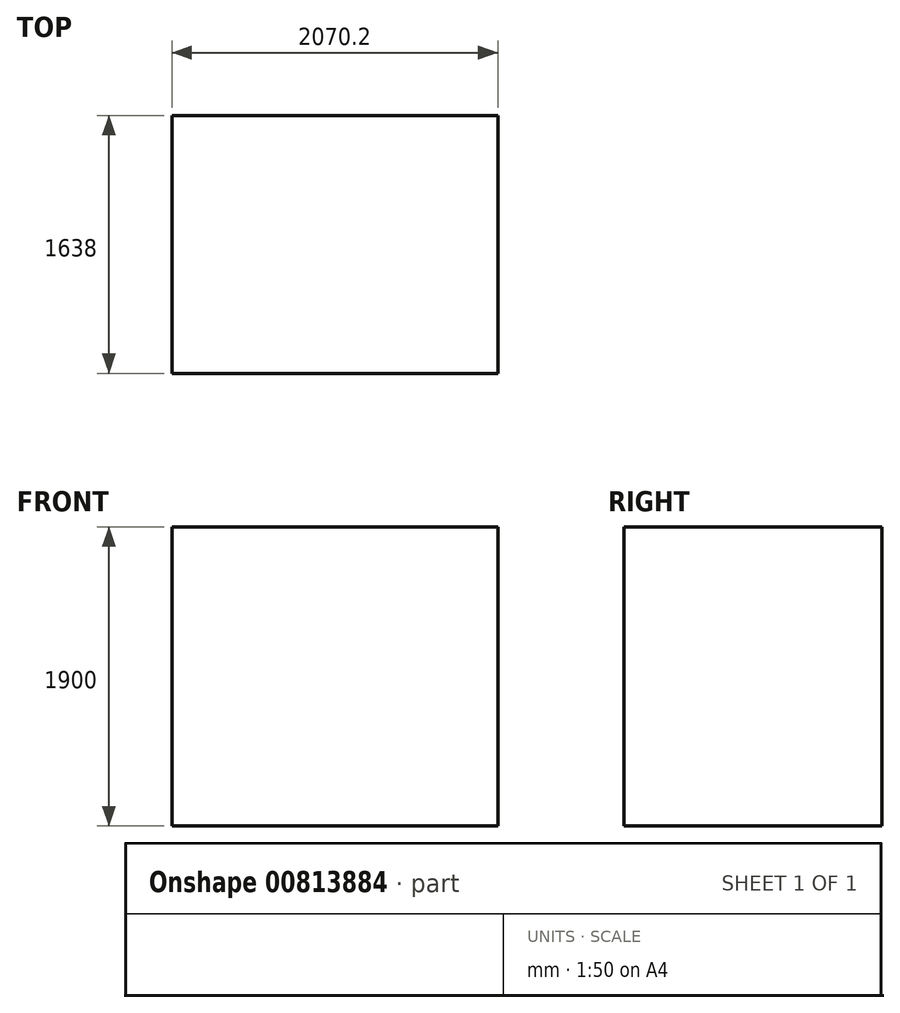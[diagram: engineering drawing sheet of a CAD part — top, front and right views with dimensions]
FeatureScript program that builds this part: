
annotation { "Feature Type Name" : "Feature", "Feature Type Description" : "" }
export const myFeature = defineFeature(function(context is Context, id is Id, definition is map)
    precondition{}
    {
        {
            var Q0;
            Q0=qCreatedBy(makeId("Front.planeOp"),FACE);
            var sketch = newSketch(context, id + "F0", { "sketchPlane" : qUnion([Q0])});
            skLineSegment(sketch, "E0.bottom", {"start": v(-1035.1, 950) * mm, "end": v(1035.1, 950) * mm});
            skLineSegment(sketch, "E0.top", {"start": v(-1035.1, -950) * mm, "end": v(1035.1, -950) * mm});
            skLineSegment(sketch, "E0.left", {"start": v(-1035.1, 950) * mm, "end": v(-1035.1, -950) * mm});
            skLineSegment(sketch, "E0.right", {"start": v(1035.1, 950) * mm, "end": v(1035.1, -950) * mm});
            skLineSegment(sketch, "E1", {"start": v(0, 4469.83) * mm, "end": v(0, -3901.9) * mm, "construction": true});
            skLineSegment(sketch, "E2", {"start": v(-3481.2, 0) * mm, "end": v(4175.35, 0) * mm, "construction": true});
            skSolve(sketch);
        }
        {
            var Q0;
            Q0 = qSketchRegion(id + "F0", true);
            extrude(context, id + "F1", {"entities" : qUnion([Q0]), "depth" : 1638 * mm, "offsetDistance" : 25.4 * mm});
        }
    });
